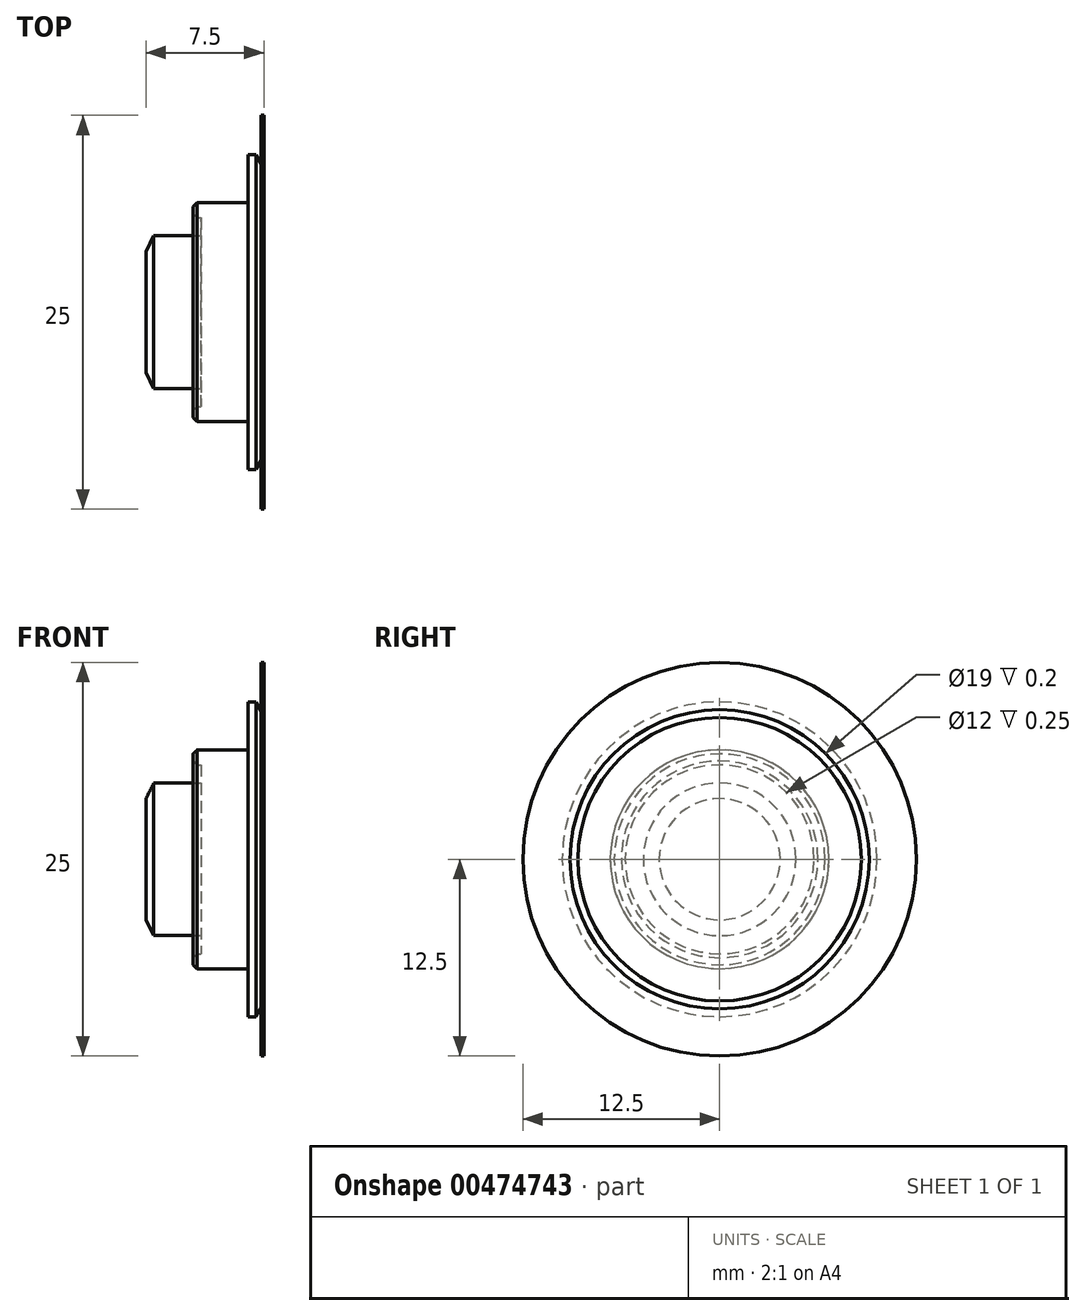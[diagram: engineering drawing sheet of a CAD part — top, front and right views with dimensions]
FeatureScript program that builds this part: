
annotation { "Feature Type Name" : "Feature", "Feature Type Description" : "" }
export const myFeature = defineFeature(function(context is Context, id is Id, definition is map)
    precondition{}
    {
        {
            var Q0;
            Q0=qCreatedBy(makeId("Right.planeOp"),FACE);
            var sketch = newSketch(context, id + "F0", { "sketchPlane" : qUnion([Q0])});
            skCircle(sketch, "E0", {"center": v(0, 0) * mm, "radius": 10 * mm});
            skSolve(sketch);
        }
        {
            var Q0;
            Q0=qSketchRegion(id+"F0",true);
            extrude(context, id + "F1", {"entities" : qUnion([Q0]), "depth" : 4 * mm, "offsetDistance" : 25 * mm});
        }
        {
            var Q0;
            Q0=makeQuery(id+"F1.opExtrude","CAP_FACE",FACE,{"disambiguationData":[OSD([sQuery(id+"F0.wireOp",EDGE,"E0")])],"isStart":true});
            var sketch = newSketch(context, id + "F2", { "sketchPlane" : qUnion([Q0])});
            skCircle(sketch, "E1", {"center": v(0, 0) * mm, "radius": 4.85 * mm});
            skSolve(sketch);
        }
        {
            var Q0;
            Q0=qSketchRegion(id+"F2",true);
            extrude(context, id + "F3", {"entities" : qUnion([Q0]), "operationType" : NewBodyOperationType.ADD, "depth" : 3.5 * mm, "offsetDistance" : 25 * mm});
        }
        {
            var Q0;
            Q0=makeQuery(id+"F1.opExtrude","CAP_FACE",FACE,{"disambiguationData":[OSD([sQuery(id+"F0.wireOp",EDGE,"E0")])],"isStart":true});
            var sketch = newSketch(context, id + "F4", { "sketchPlane" : qUnion([Q0])});
            skCircle(sketch, "E2", {"center": v(0, 0) * mm, "radius": 6.95 * mm});
            skCircle(sketch, "E3", {"center": v(0, 0) * mm, "radius": 6 * mm});
            skSolve(sketch);
        }
        {
            var Q0;
            Q0=qSketchRegion(id+"F4",true);
            extrude(context, id + "F5", {"entities" : qUnion([Q0]), "operationType" : NewBodyOperationType.ADD, "depth" : 0.5 * mm, "offsetDistance" : 25 * mm});
        }
        {
            var Q0;
            {var subQ0=sQuery(id+"F0.wireOp",EDGE,"E0");Q0=makeQuery(id+"F5.boolean.opBoolean","SPLIT",FACE,{"disambiguationData":[TD([makeQuery(id+"F1.opExtrude","SWEPT_FACE",FACE,{"disambiguationData":[OSD([subQ0])]})])],"derivedFrom":makeQuery(id+"F1.opExtrude","CAP_FACE",FACE,{"disambiguationData":[OSD([subQ0])],"isStart":true})});}
            var sketch = newSketch(context, id + "F6", { "sketchPlane" : qUnion([Q0])});
            skCircle(sketch, "E4", {"center": v(0, 0) * mm, "radius": 10 * mm});
            skCircle(sketch, "E5", {"center": v(0, 0) * mm, "radius": 6.95 * mm});
            skSolve(sketch);
        }
        {
            var Q0;
            Q0=qSketchRegion(id+"F6",true);
            extrude(context, id + "F7", {"entities" : qUnion([Q0]), "operationType" : NewBodyOperationType.REMOVE, "oppositeDirection" : true, "depth" : 3 * mm, "offsetDistance" : 25 * mm});
        }
        {
            var Q0;
            Q0=makeQuery(id+"F5.opExtrude","CAP_EDGE",EDGE,{"disambiguationData":[OSD([sQuery(id+"F4.wireOp",EDGE,"E2")])],"isStart":false});
            var Q1;
            Q1=makeQuery(id+"F5.opExtrude","CAP_EDGE",EDGE,{"disambiguationData":[OSD([sQuery(id+"F4.wireOp",EDGE,"E3")])],"isStart":false});
            chamfer(context, id + "F8", {"entities" : qUnion([Q0, Q1]), "width" : 0.25 * mm, "tangentPropagation" : true});
        }
        {
            var Q0;
            Q0=makeQuery(id+"F1.opExtrude","CAP_EDGE",EDGE,{"disambiguationData":[OSD([sQuery(id+"F0.wireOp",EDGE,"E0")])],"isStart":false});
            var Q1;
            Q1=makeQuery(id+"F3.opExtrude","CAP_EDGE",EDGE,{"disambiguationData":[OSD([sQuery(id+"F2.wireOp",EDGE,"E1")])],"isStart":false});
            chamfer(context, id + "F9", {"entities" : qUnion([Q0, Q1]), "chamferType" : ChamferType.TWO_OFFSETS, "width1" : 0.5 * mm, "oppositeDirection" : false, "width2" : 1 * mm, "tangentPropagation" : true});
        }
        {
            var Q0;
            Q0=makeQuery(id+"F1.opExtrude","CAP_FACE",FACE,{"disambiguationData":[OSD([sQuery(id+"F0.wireOp",EDGE,"E0")])],"isStart":false});
            var sketch = newSketch(context, id + "F10", { "sketchPlane" : qUnion([Q0])});
            skCircle(sketch, "E6", {"center": v(0, 0) * mm, "radius": 12.5 * mm});
            skCircle(sketch, "E7", {"center": v(0, 0) * mm, "radius": 9.5 * mm});
            skSolve(sketch);
        }
        {
            var Q0;
            Q0 = qSketchRegion(id + "F10", true);
            extrude(context, id + "F11", {"entities" : qUnion([Q0]), "operationType" : NewBodyOperationType.ADD, "oppositeDirection" : true, "depth" : 0.2 * mm, "offsetDistance" : 25 * mm});
        }
    });
